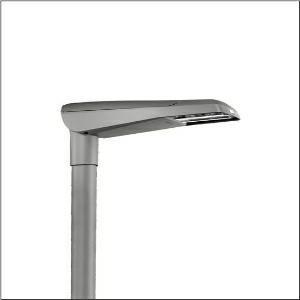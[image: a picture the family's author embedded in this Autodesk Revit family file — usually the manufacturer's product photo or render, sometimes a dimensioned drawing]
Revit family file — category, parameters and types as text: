
# Revit family: streetlight_sl_11_iq_micro___st0_5a_5xc1b51e08ce_0c76
name_source: partatom
category: Lighting Fixtures
units: mm (PartAtom-declared; Revit-internal decimal feet)

## family parameters
Cut with Voids When Loaded = No
Host = Face
Light Source = No
Part Type = Normal
Room Calculation Point = No
Round Connector Dimension = Use Diameter
Shared = No

## types (1)
- --- (1 x LED, 1860 lm, 12.6 W, 3000K)
    Apparent Load = 13 VA
    CIE Flux Codes = 42 72 97 100 100
    Color Rendering = 70
    Color Temperature = 3000K
    Default Elevation = 1800 mm
    Description = Streetlight SL 11 iQ micro, mast luminaire, primary light control with 3 zone facetted reflector, of plastic, silver coated, highly specular, primary optical cover: cover, of PMMA, transparent, light distribution: ST0.5a, light emission: direct distribution, primary light characteristic: asymmetric, installation type: post-top, side-entry, lamps: LED, High Power LED, rated values: 1.860lm | 12,6W | 147,6lm/W (begin service life); end service life: 1.860lm | 12,9W; at 50% lumin. flux: 930lm | 6,8W | 136,8lm/W, colour temperature: 3000K, colour rendering: CRI > 70, light colour: 730, light setting 1 begin service life: 100% | 1.860lm | 12,6W | 147,6lm/W | 3.000K, light setting 1 end service life: 12,9W, further light settings possible, control: optimised constant luminous flux control (CLO 2.0), Desk-Remote (wireless, voltage-free reading and setting of iQ features in the workshop via application-optimized NFC function/RFID function), Light-Fading, Smart-Wire, Night-Set, Lumen-Switch, Temp-Guard, Auto-Match, with cable H07RN-F 5x 1.5mm², mains connection: 230..240V, AC, 50/60Hz, connection cable pre-assembled, cable length: 5,5m, luminaire housing, of diecast aluminium, powder-coated, Siteco® metallic grey (DB 702S), please order mast flange separately, inclination adjustable without tools: 0°, 5°, 10°, 15° (post-top) | 0°, -5°, -10°, -15° (side-entry), sealing non-destructively replaceable, multi-level sealing system, length: 600mm, width: 174mm, height: 116mm, mast flange for spigot size: 42mm (side-entry): 5XC10008XM4, 60/48mm (side-entry/post-top): 5XC10108XM2, 76/60mm (side-entry/post-top): 5XC10108XM1, equipment: standard, protection rating (complete): IP66, insulation class (complete): insulation class II (safety insulation), certification: CE, ENEC, ENEC+, VDE, impact resistance: IK10, permissible operating ambient temperature for outdoor applications: -25..+50°C, standard-compliant lighting for roads and squares, Environmental Product Declaration (EPD) tested and certified by an independent institute, packaging unit: 1 piece

Light Distribution: ST0.5a
    Height = 116 mm
    Lamp = 1 x LED
    Lamp Light Flux = 1860 lm
    Lamp Power = 12.6 W
    Lamp count = 1
    Length = 600 mm
    Luminous efficacy = 148 lm/W
    Manufacturer = Siteco
    ModVariant = No
    Model = 5XC1B51E08CE
    Number of Poles = 1
    OnlyDefault = Yes
    Power Factor = 1
    Product Name = Streetlight SL 11 iQ micro | ST0.5a
    Product group = mast luminaire | pylon top
    ProductGroupID = 6100
    Protection Class = Protection class II
    Protection Degree = IP 66
    RLX_Detail_Level = 1
    RLX_Emergency_Light_Flux = 0 lm
    RLX_Emergency_Type = 0
    RLX_Emergency_Type_DB = No
    RlxData = <blob elided: 26813 chars, md5=30af9cb7>
    Socket = socket
    Standby Power = 0 W
    System Light Flux = 1860 lm
    System Power = 13 W
    Type Comments = factory setting: luminous flux: 100 % | dim-lin: 254 | 229 mA
    Type Image = l_1006566.jpg
    URL = http://relux.com
    VarID = @adj_003447
    Voltage = 0 V
    Weight = 0.00 kg
    Width = 174 mm

## geometry (parser evidence)
native form markers: Blend x4, Sweep x14
no freeform markers — native parametric forms only
